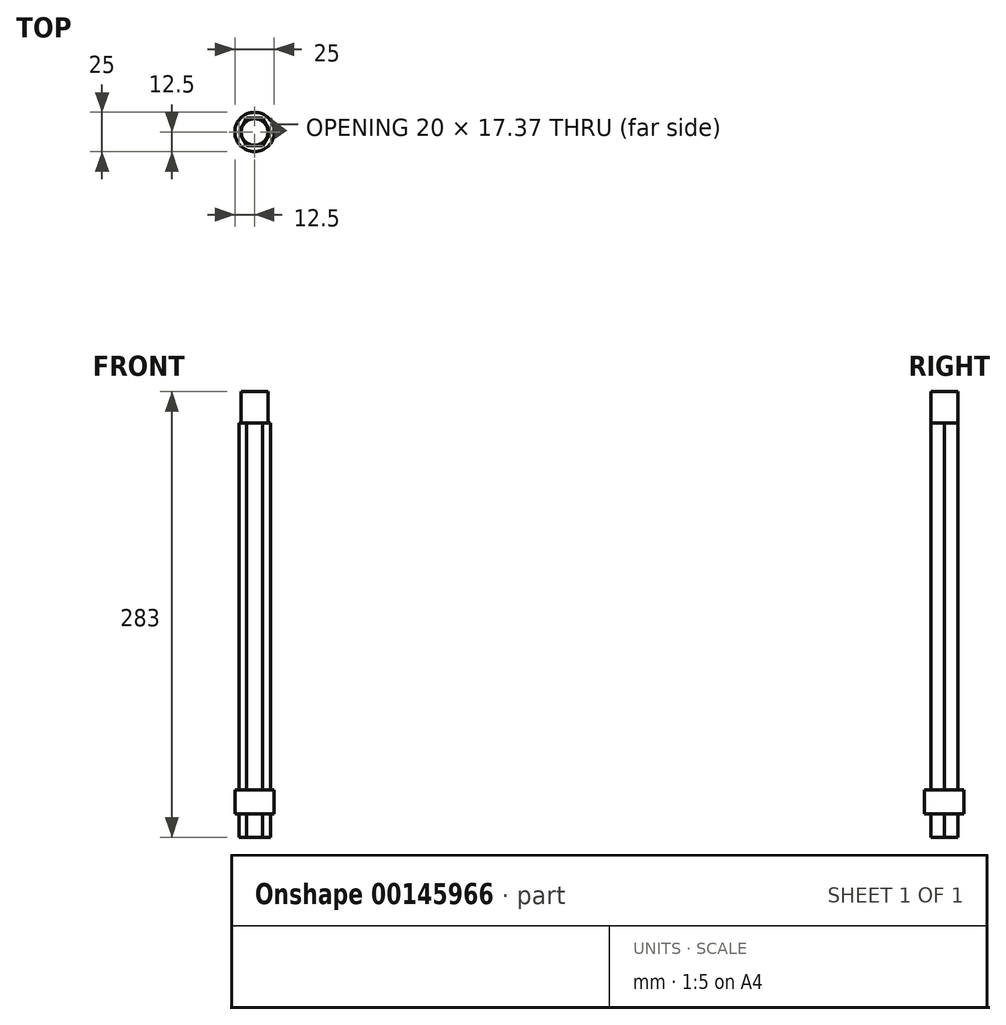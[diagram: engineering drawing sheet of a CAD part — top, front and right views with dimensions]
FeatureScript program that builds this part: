
annotation { "Feature Type Name" : "Feature", "Feature Type Description" : "" }
export const myFeature = defineFeature(function(context is Context, id is Id, definition is map)
    precondition{}
    {
        {
            var Q0;
            Q0=qCreatedBy(makeId("Top.planeOp"),FACE);
            var sketch = newSketch(context, id + "F0", { "sketchPlane" : qUnion([Q0])});
            skCircle(sketch, "E0.cCircle", {"center": v(0, 0) * mm, "radius": 8.66 * mm, "construction": true});
            skLineSegment(sketch, "E0.0", {"start": v(-5, 8.66) * mm, "end": v(5, 8.66) * mm});
            skLineSegment(sketch, "E0.1", {"start": v(5, 8.66) * mm, "end": v(10, 0) * mm});
            skLineSegment(sketch, "E0.2", {"start": v(10, 0) * mm, "end": v(5, -8.66) * mm});
            skLineSegment(sketch, "E0.3", {"start": v(5, -8.66) * mm, "end": v(-5, -8.66) * mm});
            skLineSegment(sketch, "E0.4", {"start": v(-5, -8.66) * mm, "end": v(-10, 0) * mm});
            skLineSegment(sketch, "E0.5", {"start": v(-10, 0) * mm, "end": v(-5, 8.66) * mm});
            skPoint(sketch, "E0.0.midPoint", {"position": v(0, 8.66) * mm});
            skSolve(sketch);
        }
        {
            var Q0;
            Q0=makeQuery(id+"F0.imprint","IMPRINT",FACE,{"disambiguationData":[TD([[makeQuery(id+"F0.imprint","IMPRINT",EDGE,{"derivedFrom":sQuery(id+"F0.wireOp",EDGE,"E0.0")}),-1.0]])]});
            extrude(context, id + "F1", {"entities" : qUnion([Q0]), "depth" : 233 * mm});
        }
        {
            var Q0;
            Q0=makeQuery(id+"F1.opExtrude","CAP_FACE",FACE,{"disambiguationData":[OSD([sQuery(id+"F0.wireOp",EDGE,"E0.0"),sQuery(id+"F0.wireOp",EDGE,"E0.1"),sQuery(id+"F0.wireOp",EDGE,"E0.2"),sQuery(id+"F0.wireOp",EDGE,"E0.3"),sQuery(id+"F0.wireOp",EDGE,"E0.4"),sQuery(id+"F0.wireOp",EDGE,"E0.5")])],"isStart":false});
            var sketch = newSketch(context, id + "F2", { "sketchPlane" : qUnion([Q0])});
            skCircle(sketch, "E1", {"center": v(0, 0) * mm, "radius": 8.5 * mm});
            skSolve(sketch);
        }
        {
            var Q0;
            Q0=makeQuery(id+"F2.imprint","IMPRINT",FACE,{"disambiguationData":[TD([[makeQuery(id+"F2.imprint","IMPRINT",EDGE,{"derivedFrom":sQuery(id+"F2.wireOp",EDGE,"E1")}),1.0]])]});
            extrude(context, id + "F3", {"entities" : qUnion([Q0]), "operationType" : NewBodyOperationType.ADD, "depth" : 20 * mm});
        }
        {
            var Q0;
            Q0=makeQuery(id+"F1.opExtrude","CAP_FACE",FACE,{"disambiguationData":[OSD([sQuery(id+"F0.wireOp",EDGE,"E0.0"),sQuery(id+"F0.wireOp",EDGE,"E0.1"),sQuery(id+"F0.wireOp",EDGE,"E0.2"),sQuery(id+"F0.wireOp",EDGE,"E0.3"),sQuery(id+"F0.wireOp",EDGE,"E0.4"),sQuery(id+"F0.wireOp",EDGE,"E0.5")])],"isStart":true});
            var sketch = newSketch(context, id + "F4", { "sketchPlane" : qUnion([Q0])});
            skCircle(sketch, "E2", {"center": v(0, 0) * mm, "radius": 12.5 * mm});
            skSolve(sketch);
        }
        {
            var Q0;
            Q0=makeQuery(id+"F4.imprint","IMPRINT",FACE,{"disambiguationData":[TD([[makeQuery(id+"F4.imprint","IMPRINT",EDGE,{"derivedFrom":sQuery(id+"F4.wireOp",EDGE,"E2")}),1.0]])]});
            var Q1;
            Q1=makeQuery(id+"F4.imprint","IMPRINT",FACE,{"disambiguationData":[TD([[makeQuery(id+"F4.imprint","IMPRINT",EDGE,{"derivedFrom":makeQuery(id+"F1.opExtrude","CAP_EDGE",EDGE,{"disambiguationData":[OSD([sQuery(id+"F0.wireOp",EDGE,"E0.0")])],"isStart":true})}),1.0]])]});
            extrude(context, id + "F5", {"entities" : qUnion([Q0, Q1]), "operationType" : NewBodyOperationType.ADD, "depth" : 15 * mm});
        }
        {
            var Q0;
            Q0=makeQuery(id+"F5.opExtrude","CAP_FACE",FACE,{"disambiguationData":[OSD([sQuery(id+"F4.wireOp",EDGE,"E2")])],"isStart":false});
            var sketch = newSketch(context, id + "F6", { "sketchPlane" : qUnion([Q0])});
            skCircle(sketch, "E3.cCircle", {"center": v(0, 0) * mm, "radius": 8.66 * mm, "construction": true});
            skLineSegment(sketch, "E3.0", {"start": v(10, -0.05) * mm, "end": v(4.95, -8.69) * mm});
            skLineSegment(sketch, "E3.1", {"start": v(4.95, -8.69) * mm, "end": v(-5.05, -8.63) * mm});
            skLineSegment(sketch, "E3.2", {"start": v(-5.05, -8.63) * mm, "end": v(-10, 0.05) * mm});
            skLineSegment(sketch, "E3.3", {"start": v(-10, 0.05) * mm, "end": v(-4.95, 8.69) * mm});
            skLineSegment(sketch, "E3.4", {"start": v(-4.95, 8.69) * mm, "end": v(5.05, 8.63) * mm});
            skLineSegment(sketch, "E3.5", {"start": v(5.05, 8.63) * mm, "end": v(10, -0.05) * mm});
            skPoint(sketch, "E3.0.midPoint", {"position": v(7.48, -4.37) * mm});
            skSolve(sketch);
        }
        {
            var Q0;
            Q0=makeQuery(id+"F6.imprint","IMPRINT",FACE,{"disambiguationData":[TD([[makeQuery(id+"F6.imprint","IMPRINT",EDGE,{"derivedFrom":sQuery(id+"F6.wireOp",EDGE,"E3.0")}),-1.0]])]});
            extrude(context, id + "F7", {"entities" : qUnion([Q0]), "operationType" : NewBodyOperationType.ADD, "depth" : 15 * mm});
        }
    });
